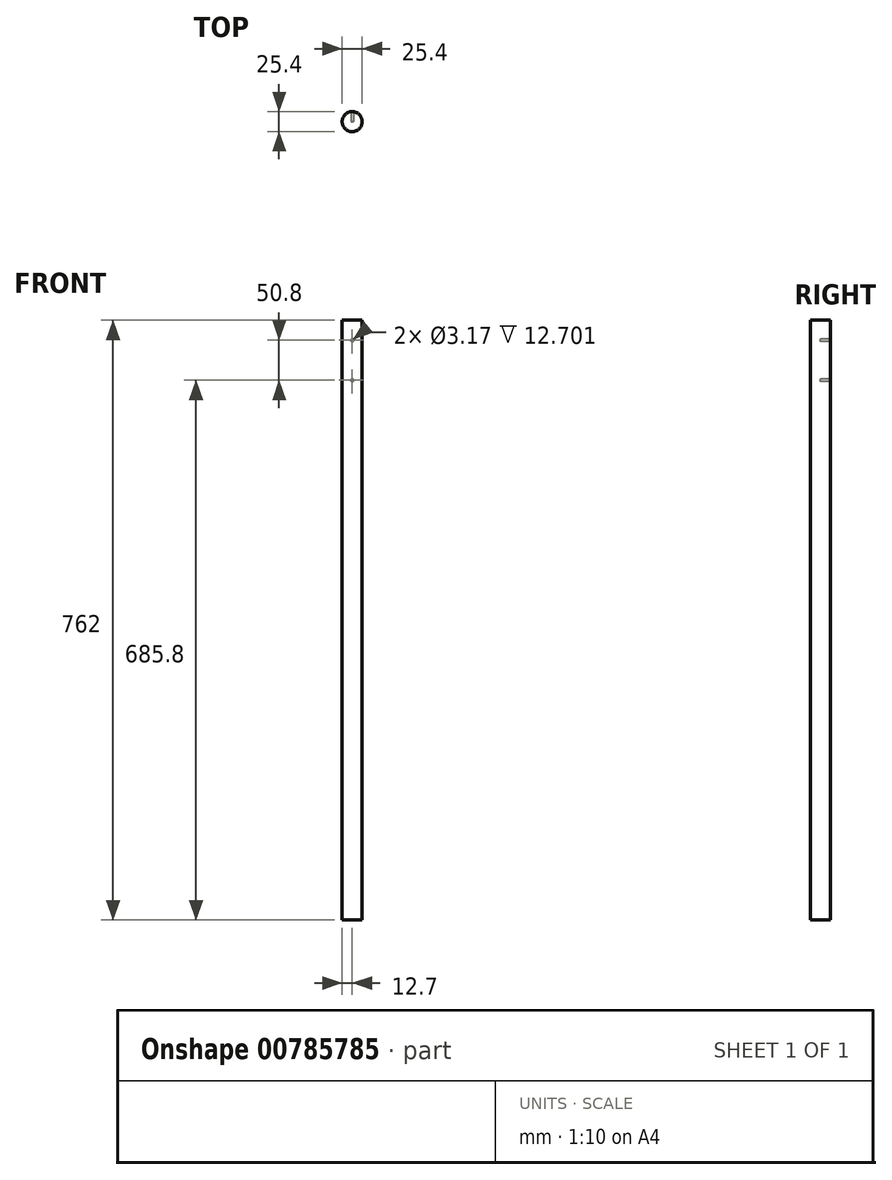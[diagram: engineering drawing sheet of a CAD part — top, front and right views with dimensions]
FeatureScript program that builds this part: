
annotation { "Feature Type Name" : "Feature", "Feature Type Description" : "" }
export const myFeature = defineFeature(function(context is Context, id is Id, definition is map)
    precondition{}
    {
        {
            var Q0;
            Q0=qCreatedBy(makeId("Top.planeOp"),FACE);
            var sketch = newSketch(context, id + "F0", { "sketchPlane" : qUnion([Q0])});
            skCircle(sketch, "E0", {"center": v(0, 0) * mm, "radius": 12.7 * mm});
            skSolve(sketch);
        }
        {
            var Q0;
            Q0=makeQuery(id+"F0.imprint","IMPRINT",FACE,{"disambiguationData":[TD([[makeQuery(id+"F0.imprint","IMPRINT",EDGE,{"derivedFrom":sQuery(id+"F0.wireOp",EDGE,"E0")}),1.0]])]});
            var Q1;
            Q1=sQuery(id+"F0.wireOp",EDGE,"E0");
            extrude(context, id + "F1", {"entities" : qUnion([Q0]), "surfaceEntities" : qUnion([Q1]), "depth" : 762 * mm, "offsetDistance" : 25.4 * mm});
        }
        {
            var Q0;
            Q0=qCreatedBy(makeId("Front.planeOp"),FACE);
            var sketch = newSketch(context, id + "F2", { "sketchPlane" : qUnion([Q0])});
            skLineSegment(sketch, "E1", {"start": v(0, 0) * mm, "end": v(0, 940.47) * mm, "construction": true});
            skPoint(sketch, "E2", {"position": v(0, 736.6) * mm});
            skPoint(sketch, "E3", {"position": v(0, 685.8) * mm});
            skSolve(sketch);
        }
        {
            var Q0;
            Q0=sQuery(id+"F2.wireOp",VERTEX,"E2");
            var Q1;
            Q1=sQuery(id+"F2.wireOp",VERTEX,"E3");
            var Q2;
            Q2=makeQuery(id+"F1.opExtrude","SWEPT_BODY",BODY,{"disambiguationData":[OSD([sQuery(id+"F0.wireOp",EDGE,"E0")])]});
            hole(context, id + "F3", {"style" : HoleStyle.SIMPLE, "endStyle" : HoleEndStyle.THROUGH, "holeDiameter" : 3.17 * mm, "majorDiameter" : 6.35 * mm, "isTappedThrough" : true, "tappedDepth" : 12.7 * mm, "tapClearance" : 3, "locations" : qUnion([Q0, Q1]), "scope" : qUnion([Q2])});
        }
    });
